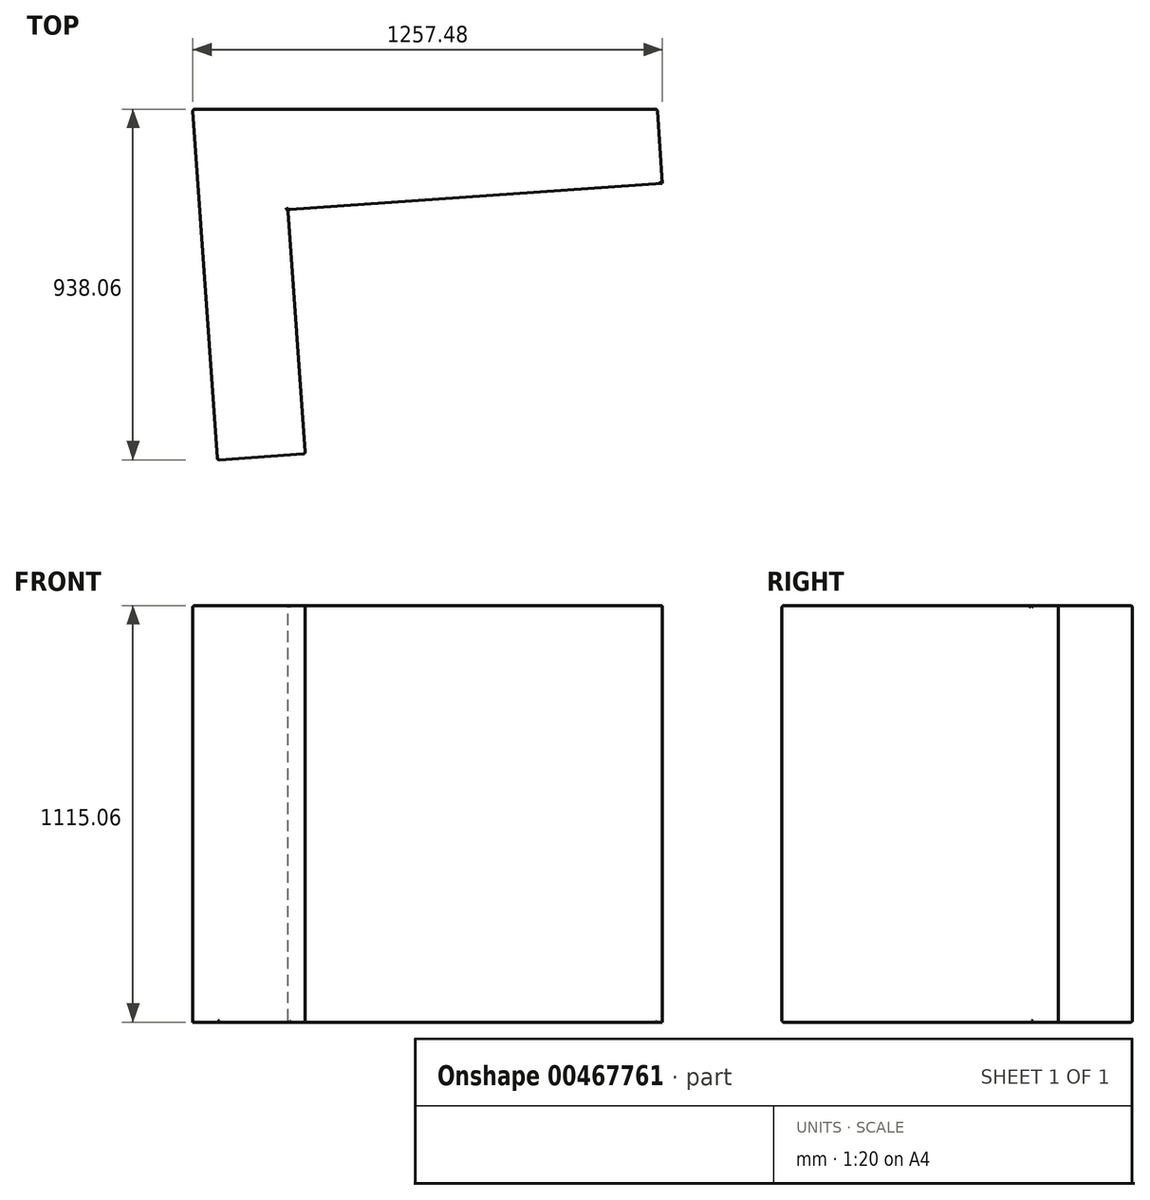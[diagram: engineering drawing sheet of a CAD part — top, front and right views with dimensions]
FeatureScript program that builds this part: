
annotation { "Feature Type Name" : "Feature", "Feature Type Description" : "" }
export const myFeature = defineFeature(function(context is Context, id is Id, definition is map)
    precondition{}
    {
        {
            var Q0;
            Q0=qCreatedBy(makeId("Top.planeOp"),FACE);
            var sketch = newSketch(context, id + "F0", { "sketchPlane" : qUnion([Q0])});
            skLineSegment(sketch, "E0", {"start": v(16.55, -826.99) * mm, "end": v(-49.65, 111.42) * mm});
            skLineSegment(sketch, "E1", {"start": v(16.55, -826.99) * mm, "end": v(251.67, -810.4) * mm});
            skLineSegment(sketch, "E2", {"start": v(251.67, -810.4) * mm, "end": v(205.62, -157.67) * mm});
            skLineSegment(sketch, "E3", {"start": v(205.62, -157.67) * mm, "end": v(1208.2, -86.93) * mm});
            skLineSegment(sketch, "E4", {"start": v(1208.2, -86.93) * mm, "end": v(1194.2, 111.42) * mm});
            skLineSegment(sketch, "E5", {"start": v(1194.2, 111.42) * mm, "end": v(-49.65, 111.42) * mm});
            skSolve(sketch);
        }
        {
            var Q0;
            Q0 = qSketchRegion(id + "F0", true);
            extrude(context, id + "F1", {"entities" : qUnion([Q0]), "depth" : 1115.06 * mm});
        }
        {
            var Q0;
            Q0=makeQuery(id+"F1.opExtrude","SWEPT_FACE",FACE,{"disambiguationData":[OSD([sQuery(id+"F0.wireOp",EDGE,"E3")])]});
            var sketch = newSketch(context, id + "F2", { "sketchPlane" : qUnion([Q0])});
            skLineSegment(sketch, "E6.bottom", {"start": v(939.75, 196.66) * mm, "end": v(763.48, 196.66) * mm});
            skLineSegment(sketch, "E6.top", {"start": v(939.75, 953.71) * mm, "end": v(763.48, 953.71) * mm});
            skLineSegment(sketch, "E6.left", {"start": v(939.75, 196.66) * mm, "end": v(939.75, 953.71) * mm});
            skLineSegment(sketch, "E6.right", {"start": v(763.48, 196.66) * mm, "end": v(763.48, 953.71) * mm});
            skSolve(sketch);
        }
        {
            var Q0;
            Q0=makeQuery(id+"F1.opExtrude","SWEPT_FACE",FACE,{"disambiguationData":[OSD([sQuery(id+"F0.wireOp",EDGE,"E1")])]});
            var Q1;
            Q1=makeQuery(id+"F1.opExtrude","CAP_FACE",FACE,{"disambiguationData":[OSD([sQuery(id+"F0.wireOp",EDGE,"E0"),sQuery(id+"F0.wireOp",EDGE,"E1"),sQuery(id+"F0.wireOp",EDGE,"E2"),sQuery(id+"F0.wireOp",EDGE,"E3"),sQuery(id+"F0.wireOp",EDGE,"E4"),sQuery(id+"F0.wireOp",EDGE,"E5")])],"isStart":false});
            fillet(context, id + "F3", {"entities" : qUnion([Q0, Q1]), "radius" : 5.08 * mm, "tangentPropagation" : true, "allowEdgeOverflow" : false});
        }
        {
            var Q0;
            {var subQ0=sQuery(id+"F0.wireOp",EDGE,"E2");Q0=makeQuery(id+"F3.opFillet","BLEND_EDGE",EDGE,{"blendedFrom":[makeQuery(id+"F1.opExtrude","SWEPT_EDGE",EDGE,{"disambiguationData":[OSD([sQuery(id+"F0.wireOp",EDGE,"E1"),subQ0])]}),makeQuery(id+"F1.opExtrude","SWEPT_FACE",FACE,{"disambiguationData":[OSD([subQ0])]})],"blendedInto":[makeQuery(id+"F1.opExtrude","SWEPT_FACE",FACE,{"disambiguationData":[OSD([subQ0])]})]});}
            var Q1;
            Q1=makeQuery(id+"F1.opExtrude","SWEPT_FACE",FACE,{"disambiguationData":[OSD([sQuery(id+"F0.wireOp",EDGE,"E2")])]});
            fillet(context, id + "F4", {"entities" : qUnion([Q0, Q1]), "radius" : 5.08 * mm, "tangentPropagation" : true, "allowEdgeOverflow" : false});
        }
        {
            var Q0;
            Q0=makeQuery(id+"F1.opExtrude","SWEPT_FACE",FACE,{"disambiguationData":[OSD([sQuery(id+"F0.wireOp",EDGE,"E5")])]});
            var Q1;
            Q1=makeQuery(id+"F1.opExtrude","CAP_FACE",FACE,{"disambiguationData":[OSD([sQuery(id+"F0.wireOp",EDGE,"E0"),sQuery(id+"F0.wireOp",EDGE,"E1"),sQuery(id+"F0.wireOp",EDGE,"E2"),sQuery(id+"F0.wireOp",EDGE,"E3"),sQuery(id+"F0.wireOp",EDGE,"E4"),sQuery(id+"F0.wireOp",EDGE,"E5")])],"isStart":false});
            fillet(context, id + "F5", {"entities" : qUnion([Q0, Q1]), "radius" : 5.08 * mm, "tangentPropagation" : true, "allowEdgeOverflow" : false});
        }
    });
